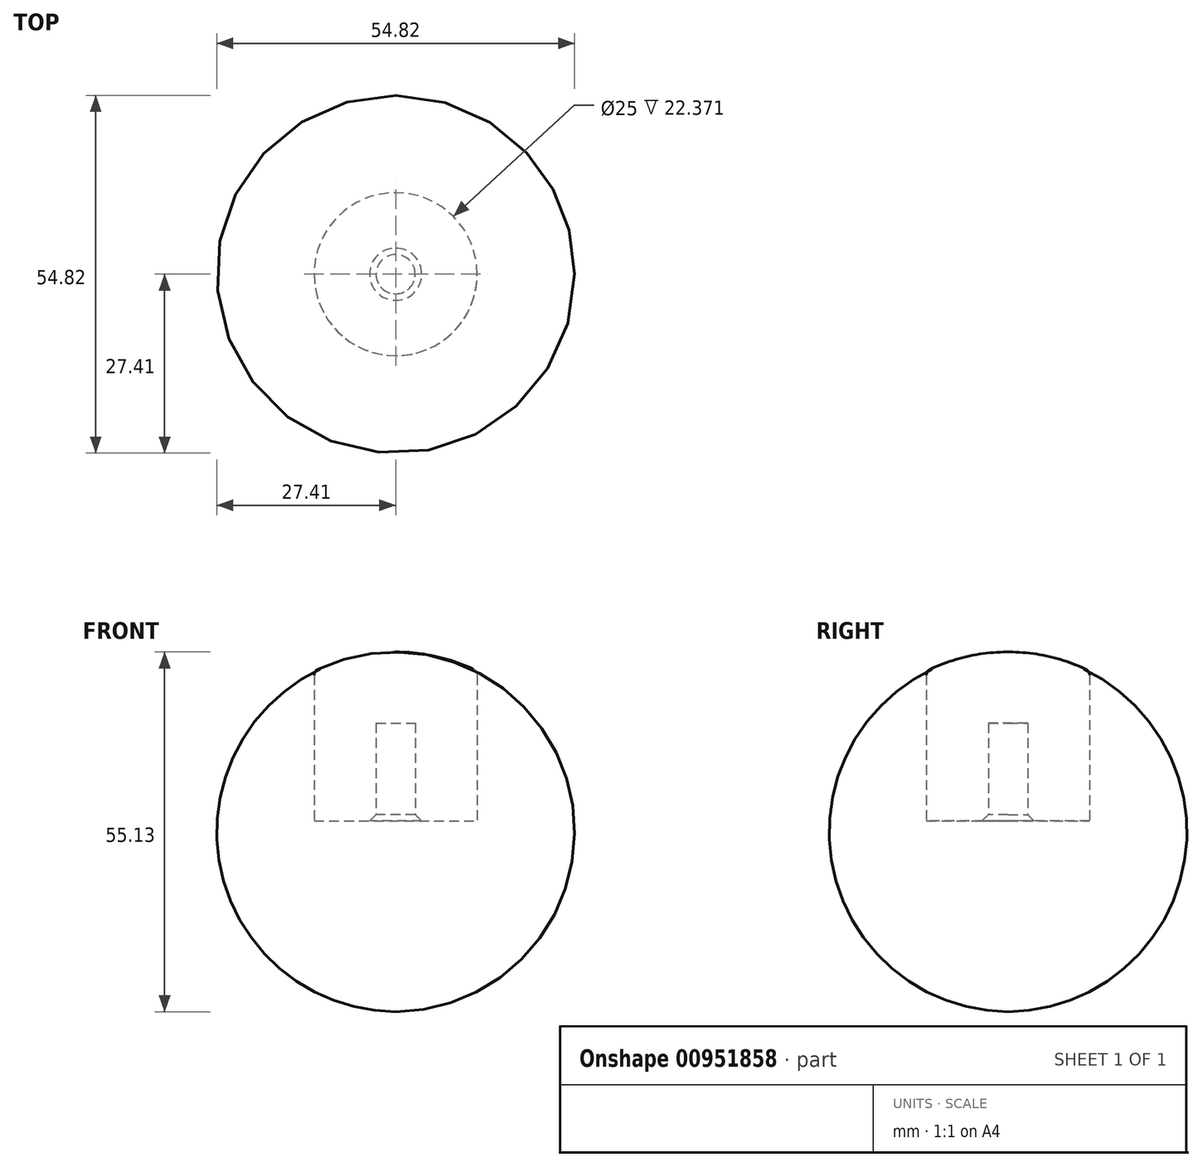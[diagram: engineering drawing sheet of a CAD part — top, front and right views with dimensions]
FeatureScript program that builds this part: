
annotation { "Feature Type Name" : "Feature", "Feature Type Description" : "" }
export const myFeature = defineFeature(function(context is Context, id is Id, definition is map)
    precondition{}
    {
        {
            var Q0;
            Q0=qCreatedBy(makeId("Front.planeOp"),FACE);
            var sketch = newSketch(context, id + "F0", { "sketchPlane" : qUnion([Q0])});
            skLineSegment(sketch, "E0", {"start": v(-12.5, 0) * mm, "end": v(-3, 0) * mm});
            skLineSegment(sketch, "E1", {"start": v(0, 15) * mm, "end": v(0, 25.91) * mm});
            skLineSegment(sketch, "E2", {"start": v(-12.5, 0) * mm, "end": v(-12.5, 23) * mm});
            skArc(sketch, "E3", {"start": v(0, 25.91) * mm, "mid": v(-6.42, 25.2) * mm, "end": v(-12.5, 23) * mm});
            skLineSegment(sketch, "E4", {"start": v(-3, 0) * mm, "end": v(-3, 15) * mm});
            skLineSegment(sketch, "E5", {"start": v(-3, 15) * mm, "end": v(0, 15) * mm});
            skSolve(sketch);
        }
        {
            var Q0;
            Q0 = qSketchRegion(id + "F0", true);
            var Q1;
            Q1=sQuery(id+"F0.wireOp",EDGE,"E1");
            revolve(context, id + "F1", {"surfaceOperationType" : NewSurfaceOperationType.NEW, "entities" : qUnion([Q0]), "axis" : qUnion([Q1]), "revolveType" : RevolveType.FULL});
        }
        {
            var Q0;
            Q0=makeQuery(id+"F1.opRevolve","SWEPT_EDGE",EDGE,{"disambiguationData":[OSD([sQuery(id+"F0.wireOp",EDGE,"E0"),sQuery(id+"F0.wireOp",EDGE,"E4")])]});
            chamfer(context, id + "F2", {"entities" : qUnion([Q0]), "width" : 1 * mm, "tangentPropagation" : true});
        }
        {
            var Q0;
            Q0=makeQuery(id+"F1.opRevolve","SWEPT_EDGE",EDGE,{"disambiguationData":[OSD([sQuery(id+"F0.wireOp",EDGE,"E2"),sQuery(id+"F0.wireOp",EDGE,"E3")])]});
            fillet(context, id + "F3", {"entities" : qUnion([Q0]), "radius" : 1 * mm, "tangentPropagation" : true, "allowEdgeOverflow" : false});
        }
    });
